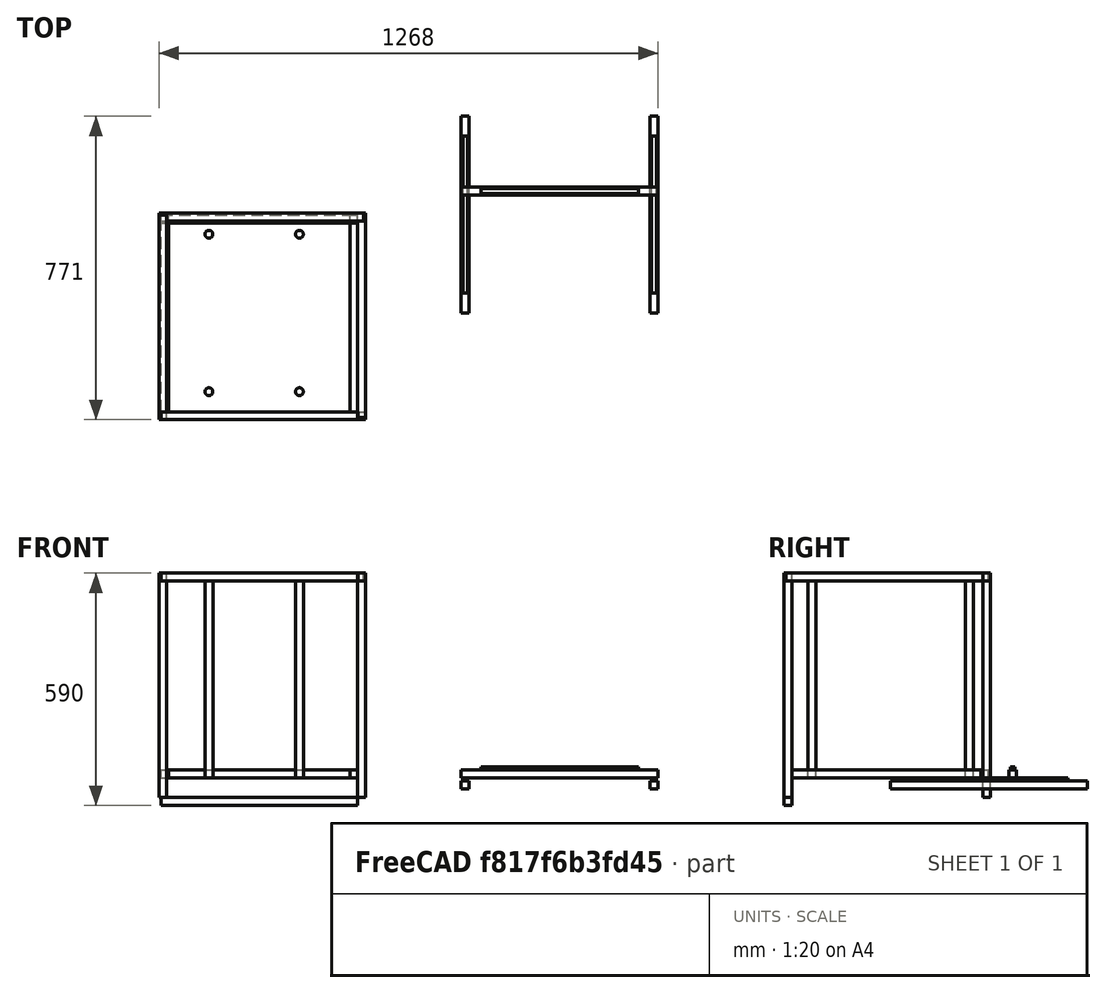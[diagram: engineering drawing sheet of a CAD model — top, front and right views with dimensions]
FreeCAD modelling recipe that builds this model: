
FCSTD DOCUMENT  (FreeCAD 0.17R13522 (Git))
Label: Estrutura
License: All rights reserved
LicenseURL: http://en.wikipedia.org/wiki/All_rights_reserved
objects: Part::Box×23, Part::Cylinder×4, App::MeasureDistance×2
note: 27 computed .brp shape members not serialized (recipe doc carries the construction recipe); baked Part::Feature solids carry a one-line shape summary decoded from their .brp

FEATURE [Part::Cylinder] Cylinder  label="Eixo guia frontal direita"
  Angle = 360
  AttacherType = Attacher::AttachEngine3D
  Height = 500
  Placement = pos=(230,0,0) rot=(0,0,1;0rad)
  Radius = 10
FEATURE [Part::Cylinder] Cylinder001  label="Eixo guia traseiro direito"
  Angle = 360
  AttacherType = Attacher::AttachEngine3D
  Height = 500
  Placement = pos=(230,400,0) rot=(0,0,1;0rad)
  Radius = 10
FEATURE [Part::Cylinder] Cylinder002  label="Eixo guia traseiro esquerdo"
  Angle = 360
  AttacherType = Attacher::AttachEngine3D
  Height = 500
  Placement = pos=(0,400,0) rot=(0,0,1;0rad)
  Radius = 10
FEATURE [Part::Cylinder] Cylinder003  label="Eixo guia frontal esquerdo"
  Angle = 360
  AttacherType = Attacher::AttachEngine3D
  Height = 500
  Radius = 10
FEATURE [Part::Box] Box  label="Vslot base frontal esquerda"
  AttacherType = Attacher::AttachEngine3D
  Height = 550
  Length = 20
  Placement = pos=(-127,-71,-50) rot=(0,0,1;0rad)
  Width = 20
FEATURE [Part::Box] Box001  label="Vslot base inferior frontal"
  AttacherType = Attacher::AttachEngine3D
  Height = 20
  Length = 500
  Placement = pos=(-122,-71,-70) rot=(0,0,1;0rad)
  Width = 20
FEATURE [Part::Box] Box002  label="Vslot base inferior traseira"
  AttacherType = Attacher::AttachEngine3D
  Height = 20
  Length = 500
  Placement = pos=(-122,429,0) rot=(0,0,1;0rad)
  Width = 20
FEATURE [Part::Box] Box003  label="Vslot base inferior esquerda"
  AttacherType = Attacher::AttachEngine3D
  Height = 20
  Length = 20
  Placement = pos=(-122,-51,0) rot=(0,0,1;0rad)
  Width = 500
FEATURE [Part::Box] Box004  label="Vslot base inferior direita"
  AttacherType = Attacher::AttachEngine3D
  Height = 20
  Length = 20
  Placement = pos=(358,-51,0) rot=(0,0,1;0rad)
  Width = 500
FEATURE [Part::Box] Box005  label="Vslot base frontal direita"
  AttacherType = Attacher::AttachEngine3D
  Height = 550
  Length = 20
  Placement = pos=(378,-71,-50) rot=(0,0,1;0rad)
  Width = 20
FEATURE [Part::Box] Box006  label="Vslot base traseira direita"
  AttacherType = Attacher::AttachEngine3D
  Height = 550
  Length = 20
  Placement = pos=(378,434,-50) rot=(0,0,1;0rad)
  Width = 20
FEATURE [Part::Box] Box007  label="Vslot base traseira esquerda"
  AttacherType = Attacher::AttachEngine3D
  Height = 550
  Length = 20
  Placement = pos=(-127,434,-50) rot=(0,0,1;0rad)
  Width = 20
FEATURE [Part::Box] Box008  label="Vslot base superior frontal"
  AttacherType = Attacher::AttachEngine3D
  Height = 20
  Length = 500
  Placement = pos=(-121,-71,500) rot=(0,0,1;0rad)
  Width = 20
FEATURE [Part::Box] Box009  label="Vslot base superior traseira"
  AttacherType = Attacher::AttachEngine3D
  Height = 20
  Length = 500
  Placement = pos=(-107,434,500) rot=(0,0,1;0rad)
  Width = 20
FEATURE [Part::Box] Box010  label="Vslot base superior direita"
  AttacherType = Attacher::AttachEngine3D
  Height = 20
  Length = 20
  Placement = pos=(378,-66,500) rot=(0,0,1;0rad)
  Width = 500
FEATURE [Part::Box] Box011  label="Cantoneira001"
  AttacherType = Attacher::AttachEngine3D
  Height = 20
  Length = 20
  Placement = pos=(-127,449,500) rot=(0,0,1;0rad)
  Width = 5
FEATURE [Part::Box] Box012  label="Vslot base superior esquerda"
  AttacherType = Attacher::AttachEngine3D
  Height = 20
  Length = 20
  Placement = pos=(-127,-51,500) rot=(0,0,1;0rad)
  Width = 500
FEATURE [Part::Box] Box013  label="Cantoneira004"
  AttacherType = Attacher::AttachEngine3D
  Height = 20
  Length = 20
  Placement = pos=(378,-71,500) rot=(0,0,1;0rad)
  Width = 5
FEATURE [Part::Box] Box014  label="Cantoneira002"
  AttacherType = Attacher::AttachEngine3D
  Height = 20
  Length = 5
  Placement = pos=(393,434,500) rot=(0,0,1;0rad)
  Width = 20
FEATURE [Part::Box] Box015  label="Cantoneira003"
  AttacherType = Attacher::AttachEngine3D
  Height = 20
  Length = 5
  Placement = pos=(-127,-71,500) rot=(0,0,1;0rad)
  Width = 20
FEATURE [Part::Box] Box016  label="Vslot Y Esquerdo"
  AttacherType = Attacher::AttachEngine3D
  Height = 20
  Length = 20
  Placement = pos=(641,200,-27.8) rot=(0,0,1;0rad)
  Width = 500
FEATURE [Part::Box] Box017  label="Vslot Y Direito"
  AttacherType = Attacher::AttachEngine3D
  Height = 20
  Length = 20
  Placement = pos=(1121,200,-27.8) rot=(0,0,1;0rad)
  Width = 500
FEATURE [Part::Box] Box018  label="Vslot X"
  AttacherType = Attacher::AttachEngine3D
  Height = 20
  Length = 500
  Placement = pos=(641,500,0) rot=(0,0,1;0rad)
  Width = 20
FEATURE [Part::Box] Box019  label="Rail X superior"
  AttacherType = Attacher::AttachEngine3D
  Height = 7.8
  Length = 400
  Placement = pos=(691,503.8,20) rot=(0,0,1;0rad)
  Width = 12.2
FEATURE [Part::Box] Box020  label="Rail Y Esquerdo"
  AttacherType = Attacher::AttachEngine3D
  Height = 7.8
  Length = 12.2
  Placement = pos=(645,250,-7.8) rot=(0,0,1;0rad)
  Width = 400
FEATURE [Part::Box] Box021  label="Rail Y Direito"
  AttacherType = Attacher::AttachEngine3D
  Height = 7.8
  Length = 12.2
  Placement = pos=(1125,250,-7.8) rot=(0,0,1;0rad)
  Width = 400
FEATURE [App::MeasureDistance] Distance  label="Distance: 20,00 mm"
  Distance = 20.0012
  P1 = (621,510.017,20)
  P2 = (641,509.801,20)
FEATURE [App::MeasureDistance] Distance001  label="Distance: 20,00 mm001"
  Distance = 20.0002
  P1 = (1121,510.985,20)
  P2 = (1141,511.078,20)
FEATURE [Part::Box] Box022  label="Vslot Y Esquerdo001"
  AttacherType = Attacher::AttachEngine3D
  Height = 20
  Length = 20
  Placement = pos=(641,200,-27.8) rot=(0,0,1;0rad)
  Width = 500
